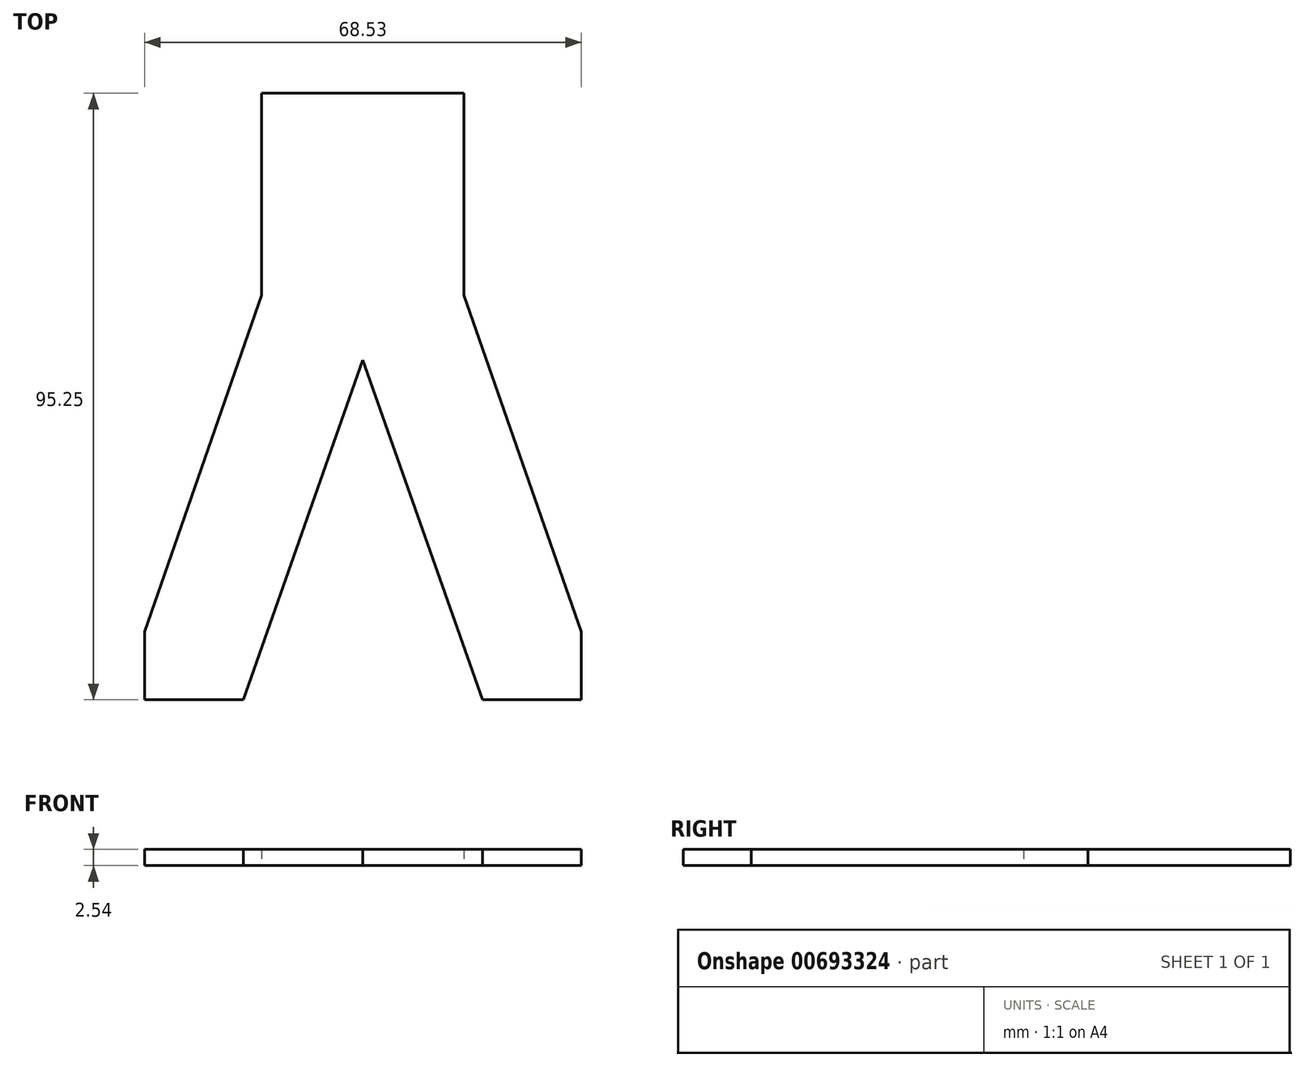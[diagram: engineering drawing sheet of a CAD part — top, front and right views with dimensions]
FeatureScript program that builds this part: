
annotation { "Feature Type Name" : "Feature", "Feature Type Description" : "" }
export const myFeature = defineFeature(function(context is Context, id is Id, definition is map)
    precondition{}
    {
        {
            var Q0;
            Q0=qCreatedBy(makeId("Top.planeOp"),FACE);
            var sketch = newSketch(context, id + "F0", { "sketchPlane" : qUnion([Q0])});
            skLineSegment(sketch, "E0", {"start": v(12.48, -31.73) * mm, "end": v(27.97, -31.73) * mm});
            skLineSegment(sketch, "E1", {"start": v(27.97, -31.73) * mm, "end": v(27.97, -21.06) * mm});
            skLineSegment(sketch, "E2", {"start": v(-40.56, -31.73) * mm, "end": v(-40.56, -21.06) * mm});
            skLineSegment(sketch, "E3", {"start": v(-40.56, -21.06) * mm, "end": v(-22.17, 31.77) * mm});
            skLineSegment(sketch, "E4", {"start": v(27.97, -21.06) * mm, "end": v(9.58, 31.77) * mm});
            skLineSegment(sketch, "E5", {"start": v(-22.17, 31.77) * mm, "end": v(-22.17, 63.52) * mm});
            skLineSegment(sketch, "E6", {"start": v(9.58, 63.52) * mm, "end": v(9.58, 31.77) * mm});
            skLineSegment(sketch, "E7", {"start": v(9.58, 63.52) * mm, "end": v(-22.17, 63.52) * mm});
            skLineSegment(sketch, "E8", {"start": v(-25.06, -31.73) * mm, "end": v(-6.3, 21.66) * mm});
            skLineSegment(sketch, "E9", {"start": v(12.48, -31.73) * mm, "end": v(-6.3, 21.66) * mm});
            skLineSegment(sketch, "E10", {"start": v(-40.56, -31.73) * mm, "end": v(-25.06, -31.73) * mm});
            skSolve(sketch);
        }
        {
            var Q0;
            Q0=makeQuery(id+"F0.imprint","IMPRINT",FACE,{"disambiguationData":[TD([[makeQuery(id+"F0.imprint","IMPRINT",EDGE,{"derivedFrom":sQuery(id+"F0.wireOp",EDGE,"E0")}),1.0]])]});
            extrude(context, id + "F1", {"entities" : qUnion([Q0]), "depth" : 2.54 * mm, "offsetDistance" : 25.4 * mm});
        }
    });
